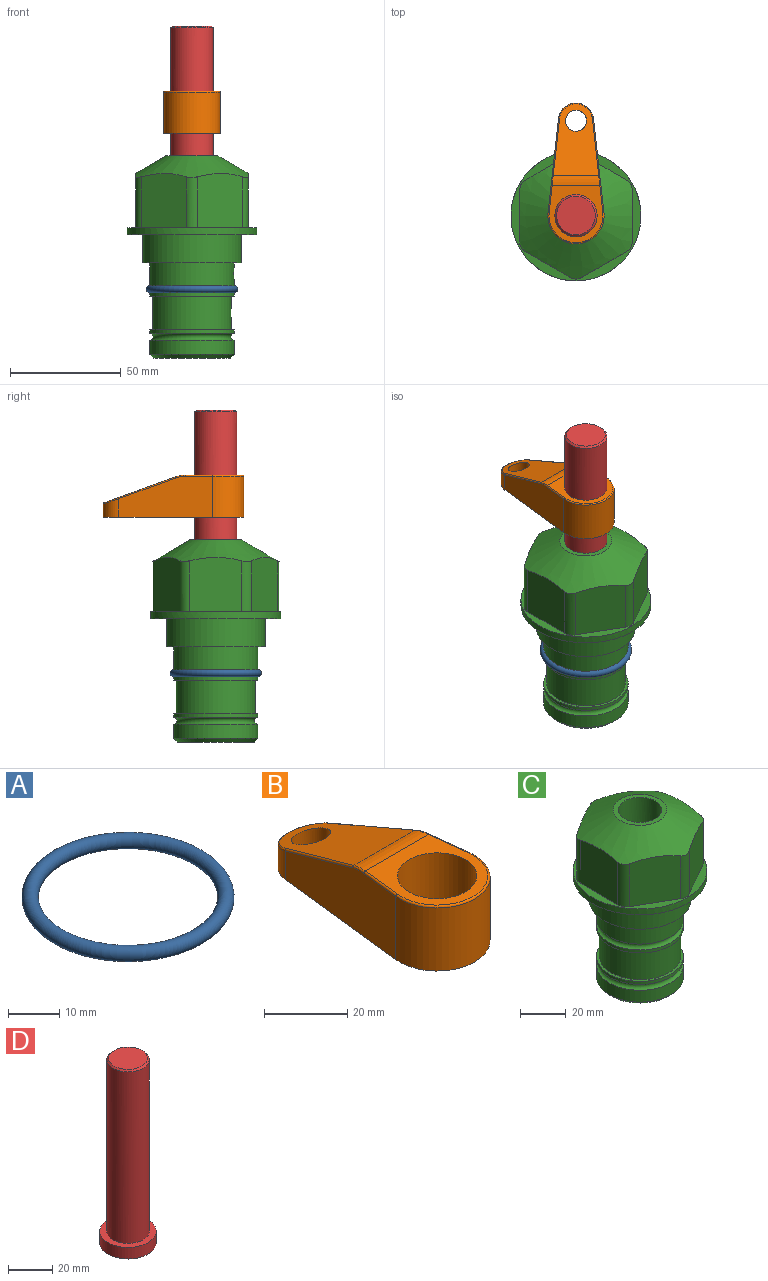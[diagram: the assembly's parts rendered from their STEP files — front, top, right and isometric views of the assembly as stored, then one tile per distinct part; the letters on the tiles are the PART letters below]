
ASSEMBLY  parts=4 mates=2
PART A: 1 faces, bbox 44.7x44.7x3.2 mm
  f0: torus R=19.05mm, axis (0,0,1), area 1193.9mm2
PART B: 44 faces, bbox 27.5x64.5x19.1 mm
  f0: plane 2.3x0.95mm, normal (0,0,-1), area 1mm2, adj f25,f30,f34
  f1: plane 63.5x25.4mm, normal (0,0,-1), area 561.7mm2, adj f2,f3,f4,f5,f6,f7,f19,f20
  f2: cylinder r=12.7mm len=25.4mm, axis (0,0,-1), area 792.2mm2, adj f1,f3,f5,f13
  f3: plane 42.33x18.54mm, normal (0.99,0.11,0), area 647mm2, adj f1,f2,f4,f11,f12,f14
  f4: cylinder r=7.94mm len=15.78mm, axis (0,0,-1), area 158.6mm2, adj f1,f3,f5,f16
  f5: plane 42.33x18.54mm, normal (-0.99,0.11,0), area 647mm2, adj f1,f2,f4,f15,f17,f18
  f6: cylinder r=9.53mm len=19.05mm, axis (0,0,-1), area 1140.1mm2, adj f1,f8
  f7: cylinder r=4.76mm len=10.98mm, axis (0,0,-1), area 276.1mm2, adj f1,f9
  f8: plane 25.83x24.38mm, normal (0,0,1), area 262.2mm2, adj f6,f10,f11,f13,f15
  f9: plane 32.49x20.55mm, normal (0,0.34,0.94), area 489.9mm2, adj f7,f10,f14,f16,f18
  f10: cylinder r=12.7mm len=21.49mm, axis (-1,0,0), area 93.2mm2, adj f8,f9,f12,f17
  f11: cylinder r=0.51mm len=12.34mm, axis (0.11,-0.99,0), area 9.9mm2, adj f3,f8,f12,f13
  f12: bspline ~7.62x1.64mm, area 3.5mm2, adj f3,f10,f11,f14
  f13: torus R=12.19mm, axis (0,0,1), area 33.6mm2, adj f2,f8,f11,f15
  f14: cylinder r=0.51mm len=26.01mm, axis (0.1,-0.93,0.34), area 21.6mm2, adj f3,f9,f12,f16
  f15: cylinder r=0.51mm len=12.34mm, axis (0.11,0.99,0), area 9.9mm2, adj f5,f8,f13,f17
  f16: bspline ~15.78x7.05mm, area 15.7mm2, adj f4,f9,f14,f18
  f17: bspline ~7.62x1.64mm, area 3.5mm2, adj f5,f10,f15,f18
  f18: cylinder r=0.51mm len=26.01mm, axis (0.1,0.93,-0.34), area 21.6mm2, adj f5,f9,f16,f17
  f19: plane 21.6x14.29mm, normal (-0.99,-0.11,0), area 242.6mm2, adj f1,f26,f28,f34,f36,f38
  f20: plane 21.6x14.29mm, normal (0.99,-0.11,0), area 242.6mm2, adj f1,f27,f29,f37,f39,f41
  f21: cylinder r=12.7mm len=14.29mm, axis (0,0,-1), area 173.2mm2, adj f1,f26,f27,f30,f31,f33
  f22: cylinder r=7.94mm len=7.63mm, axis (0,0,-1), area 53.8mm2, adj f1,f28,f29,f42
  f23: plane 2.3x0.95mm, normal (0,0,-1), area 1mm2, adj f25,f33,f37
  f24: plane 17.94x12.32mm, normal (0,-0.34,-0.94), area 191.2mm2, adj f25,f38,f41,f42
  f25: cylinder r=9.53mm len=12.93mm, axis (-1,0,0), area 37.5mm2, adj f0,f23,f24,f31,f36,f39
  f26: cylinder r=1.59mm len=14.29mm, axis (0,0,-1), area 49mm2, adj f1,f19,f21,f32
  f27: cylinder r=1.59mm len=14.29mm, axis (0,0,-1), area 49mm2, adj f1,f20,f21,f35
  f28: cylinder r=1.59mm len=7.28mm, axis (0,0,-1), area 22.1mm2, adj f1,f19,f22,f40
  f29: cylinder r=1.59mm len=7.28mm, axis (0,0,-1), area 22.1mm2, adj f1,f20,f22,f43
  f30: torus R=14.29mm, axis (0,0,1), area 5.8mm2, adj f0,f21,f31,f32
  f31: bspline ~11.06x2.73mm, area 20.8mm2, adj f21,f25,f30,f33
  f32: sphere r=1.59mm, area 5.4mm2, adj f26,f30,f34
  f33: torus R=14.29mm, axis (0,0,1), area 5.8mm2, adj f21,f23,f31,f35
  f34: cylinder r=1.59mm len=1.68mm, axis (-0.11,0.99,0), area 2.4mm2, adj f0,f19,f32,f36
  f35: sphere r=1.59mm, area 5.4mm2, adj f27,f33,f37
  f36: bspline ~5.82x2.33mm, area 7.7mm2, adj f19,f25,f34,f38
  f37: cylinder r=1.59mm len=1.68mm, axis (0.11,0.99,0), area 2.4mm2, adj f20,f23,f35,f39
  f38: cylinder r=1.59mm len=18.33mm, axis (0.1,-0.93,0.34), area 46.7mm2, adj f19,f24,f36,f40
  f39: bspline ~5.82x2.33mm, area 7.7mm2, adj f20,f25,f37,f41
  f40: sphere r=1.59mm, area 3.6mm2, adj f28,f38,f42
  f41: cylinder r=1.59mm len=18.33mm, axis (0.1,0.93,-0.34), area 46.7mm2, adj f20,f24,f39,f43
  f42: bspline ~8.31x1.84mm, area 15.3mm2, adj f22,f24,f40,f43
  f43: sphere r=1.59mm, area 3.6mm2, adj f29,f41,f42
PART C: 36 faces, bbox 58.7x58.7x91.2 mm
  f0: cylinder r=17.78mm len=35.56mm, axis (0,0,1), area 1670.8mm2, adj f23,f24,f31
  f1: cylinder r=19.05mm len=38.1mm, axis (0,0,1), area 1191.9mm2, adj f26,f27,f30
  f2: plane 58.66x58.66mm, normal (0,0,-1), area 1150.6mm2, adj f3,f28
  f3: cylinder r=29.33mm len=58.66mm, axis (0,0,-1), area 585.1mm2, adj f2,f4
  f4: plane 58.66x58.66mm, normal (0,0,1), area 475.9mm2, adj f3,f5,f6,f7,f8,f9,f10,f11
  f5: plane 24.5x20.32mm, normal (-0.5,0.87,0), area 562.8mm2, adj f4,f15,f16,f17
  f6: plane 24.5x20.32mm, normal (0.5,0.87,0), area 562.8mm2, adj f4,f14,f15,f17
  f7: plane 24.5x23.48mm, normal (1,0,0), area 562.8mm2, adj f4,f13,f14,f17
  f8: plane 24.5x20.32mm, normal (0.5,-0.87,0), area 562.8mm2, adj f4,f12,f13,f17
  f9: plane 24.5x20.32mm, normal (-0.5,-0.87,0), area 562.8mm2, adj f4,f11,f12,f17
  f10: plane 24.5x23.48mm, normal (-1,0,0), area 562.8mm2, adj f4,f11,f16,f17
  f11: cylinder r=5.08mm len=23.01mm, axis (0,0,-1), area 121.2mm2, adj f4,f9,f10,f17
  f12: cylinder r=5.08mm len=23.01mm, axis (0,0,-1), area 121.2mm2, adj f4,f8,f9,f17
  f13: cylinder r=5.08mm len=23.01mm, axis (0,0,-1), area 121.2mm2, adj f4,f7,f8,f17
  f14: cylinder r=5.08mm len=23.01mm, axis (0,0,-1), area 121.2mm2, adj f4,f6,f7,f17
  f15: cylinder r=5.08mm len=23.01mm, axis (0,0,-1), area 121.2mm2, adj f4,f5,f6,f17
  f16: cylinder r=5.08mm len=23.01mm, axis (0,0,-1), area 121.2mm2, adj f4,f5,f10,f17
  f17: cone r=11.73mm half-angle=60deg, axis (0,0,-1), area 2071.8mm2, adj f5,f6,f7,f8,f9,f10,f11,f12
  f18: plane 23.46x23.46mm, normal (0,0,1), area 147.4mm2, adj f17,f35
  f19: plane 34.93x34.93mm, normal (0,0,-1), area 958mm2, adj f29
  f20: cylinder r=19.05mm len=38.1mm, axis (0,0,1), area 760.1mm2, adj f21,f29
  f21: torus R=19.05mm, axis (0,0,1), area 565.3mm2, adj f20,f22
  f22: cylinder r=19.05mm len=38.1mm, axis (0,0,1), area 190mm2, adj f21,f23
  f23: plane 38.1x38.1mm, normal (0,0,1), area 146.9mm2, adj f0,f22
  f24: plane 38.1x38.1mm, normal (0,0,-1), area 146.9mm2, adj f0,f25
  f25: cylinder r=19.05mm len=38.1mm, axis (0,0,1), area 190mm2, adj f24,f26
  f26: torus R=19.05mm, axis (0,0,1), area 565.3mm2, adj f1,f25
  f27: plane 44.45x44.45mm, normal (0,0,-1), area 411.7mm2, adj f1,f28
  f28: cylinder r=22.23mm len=44.45mm, axis (0,0,1), area 1773.5mm2, adj f2,f27
  f29: cone r=19.05mm half-angle=45deg, axis (0,0,1), area 257.5mm2, adj f19,f20
  f30: cylinder r=3.17mm len=6.75mm, axis (-1,0,0), area 128mm2, adj f1,f33
  f31: cylinder r=3.17mm len=6.35mm, axis (-1,0,0), area 102.5mm2, adj f0,f33
  f32: plane 25.4x25.4mm, normal (0,0,1), area 506.7mm2, adj f33
  f33: cylinder r=12.7mm len=66.42mm, axis (0,0,-1), area 5236.2mm2, adj f30,f31,f32,f34
  f34: cone r=9.53mm half-angle=30deg, axis (0,0,-1), area 443.4mm2, adj f33,f35
  f35: cylinder r=9.53mm len=19.05mm, axis (0,0,-1), area 849mm2, adj f18,f34
PART D: 6 faces, bbox 25.4x25.4x101.6 mm
  f0: plane 17.46x17.46mm, normal (0,0,1), area 239.5mm2, adj f5
  f1: plane 25.4x25.4mm, normal (0,0,-1), area 506.7mm2, adj f2
  f2: cylinder r=12.7mm len=25.4mm, axis (0,0,1), area 506.7mm2, adj f1,f3
  f3: plane 25.4x25.4mm, normal (0,0,1), area 221.7mm2, adj f2,f4
  f4: cylinder r=9.53mm len=94.46mm, axis (0,0,1), area 5653mm2, adj f3,f5
  f5: cone r=8.73mm half-angle=45deg, axis (0,0,-1), area 64.4mm2, adj f0,f4
PLACE A at identity
PLACE B t=(0,0,45.82)mm
PLACE C at identity fixed
PLACE D t=(0,0,20.56)mm
MATE slider D.f2 <-> C.f0  axis (0,0,1) through (0,0,46.2)mm
MATE slider B.f2 <-> D.f2  axis (0,0,-1) through (0,0,55.34)mm
